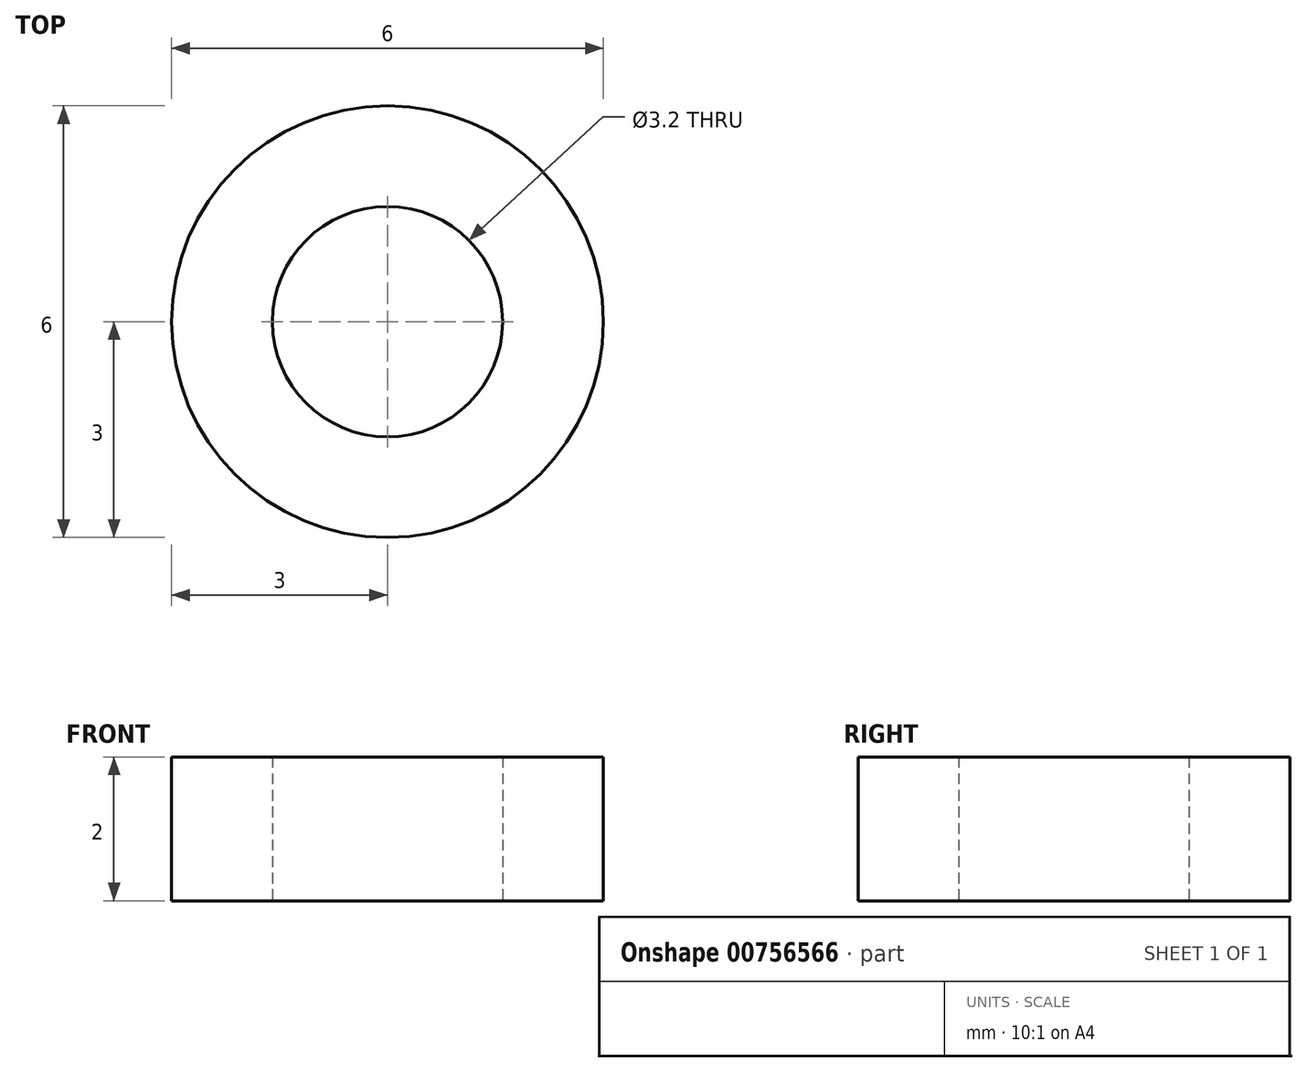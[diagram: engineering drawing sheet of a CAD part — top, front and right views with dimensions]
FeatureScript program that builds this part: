
annotation { "Feature Type Name" : "Feature", "Feature Type Description" : "" }
export const myFeature = defineFeature(function(context is Context, id is Id, definition is map)
    precondition{}
    {
        {
            var Q0;
            Q0=qCreatedBy(makeId("Top.planeOp"),FACE);
            var sketch = newSketch(context, id + "F0", { "sketchPlane" : qUnion([Q0])});
            skCircle(sketch, "E0", {"center": v(0, 0) * mm, "radius": 3 * mm});
            skCircle(sketch, "E1", {"center": v(0, 0) * mm, "radius": 1.6 * mm});
            skSolve(sketch);
        }
        {
            var Q0;
            Q0=makeQuery(id+"F0.imprint","IMPRINT",FACE,{"disambiguationData":[TD([[makeQuery(id+"F0.imprint","IMPRINT",EDGE,{"derivedFrom":sQuery(id+"F0.wireOp",EDGE,"E0")}),1.0]])]});
            extrude(context, id + "F1", {"entities" : qUnion([Q0]), "depth" : 2 * mm, "offsetDistance" : 25 * mm});
        }
    });
